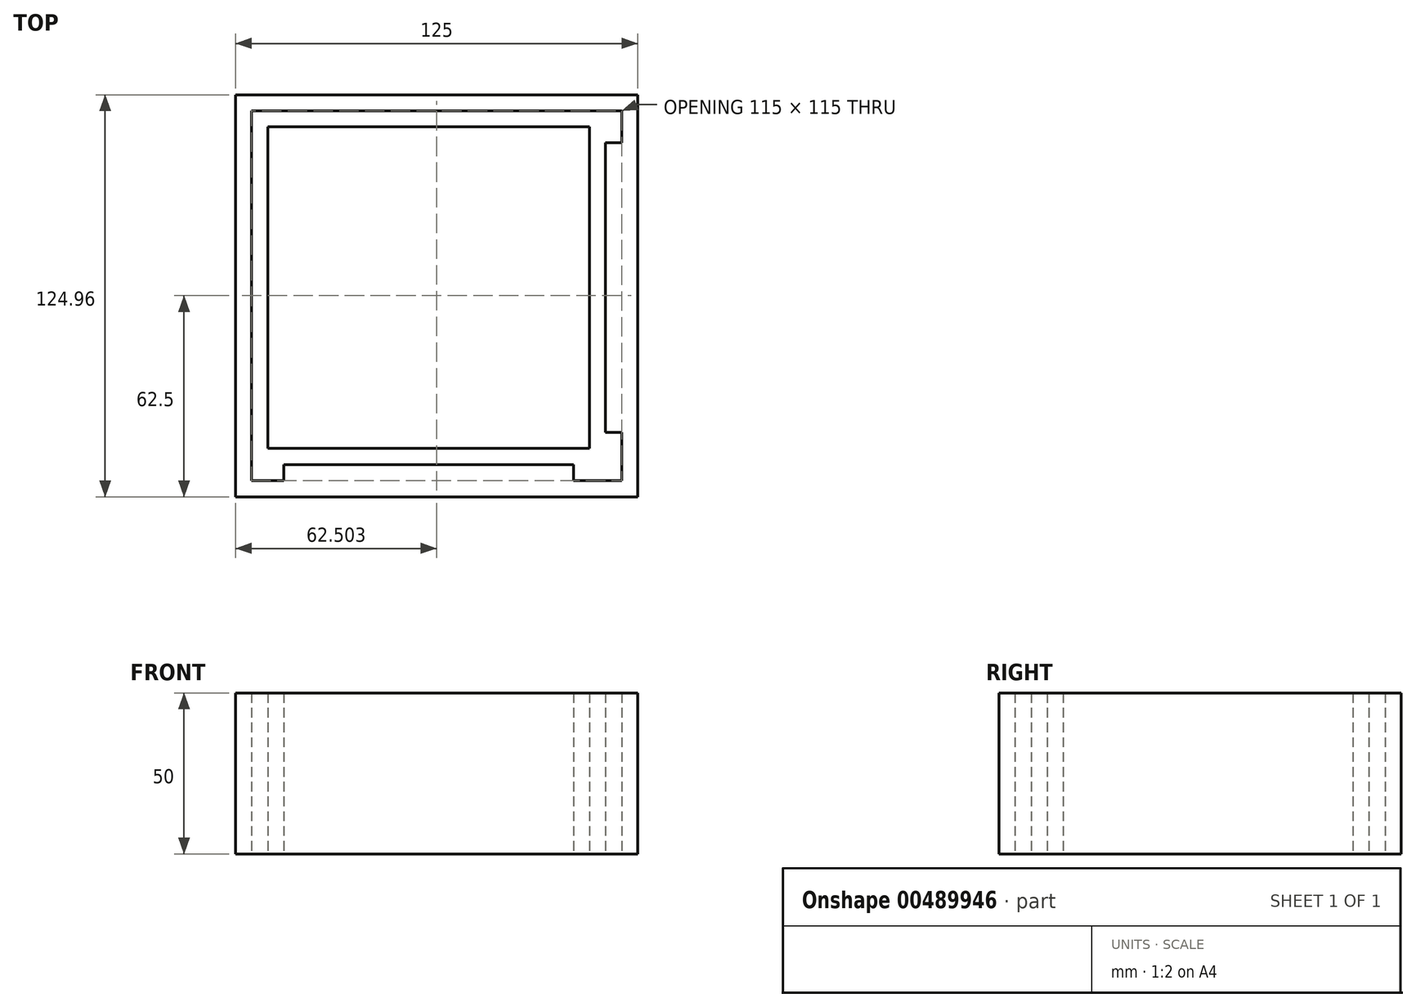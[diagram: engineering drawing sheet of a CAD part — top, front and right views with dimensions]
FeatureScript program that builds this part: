
annotation { "Feature Type Name" : "Feature", "Feature Type Description" : "" }
export const myFeature = defineFeature(function(context is Context, id is Id, definition is map)
    precondition{}
    {
        {
            var Q0;
            Q0=qCreatedBy(makeId("Top.planeOp"),FACE);
            var sketch = newSketch(context, id + "F0", { "sketchPlane" : qUnion([Q0])});
            skLineSegment(sketch, "E0.bottom", {"start": v(104.56, 35.9) * mm, "end": v(204.56, 35.9) * mm});
            skLineSegment(sketch, "E0.top", {"start": v(104.56, -64.1) * mm, "end": v(204.56, -64.1) * mm});
            skLineSegment(sketch, "E0.left", {"start": v(104.56, 35.9) * mm, "end": v(104.56, -64.1) * mm});
            skLineSegment(sketch, "E0.right", {"start": v(204.56, 35.9) * mm, "end": v(204.56, -64.1) * mm});
            skPoint(sketch, "E1", {"position": v(154.56, 35.9) * mm});
            skPoint(sketch, "E2", {"position": v(104.56, -14.1) * mm});
            skPoint(sketch, "E3", {"position": v(204.56, -14.1) * mm});
            skPoint(sketch, "E4", {"position": v(154.56, -64.1) * mm});
            skLineSegment(sketch, "E5", {"start": v(104.56, 35.9) * mm, "end": v(204.56, -64.1) * mm});
            skSolve(sketch);
        }
        {
            var Q0;
            Q0=qCreatedBy(makeId("Top.planeOp"),FACE);
            var sketch = newSketch(context, id + "F1", { "sketchPlane" : qUnion([Q0])});
            skLineSegment(sketch, "E6.bottom", {"start": v(99.56, 40.9) * mm, "end": v(214.56, 40.9) * mm});
            skLineSegment(sketch, "E6.left", {"start": v(99.56, 40.9) * mm, "end": v(99.56, -74.1) * mm});
            skPoint(sketch, "E7", {"position": v(154.56, -69.1) * mm});
            skPoint(sketch, "E8", {"position": v(159.56, 40.9) * mm});
            skLineSegment(sketch, "E9.bottom", {"start": v(209.56, 30.9) * mm, "end": v(214.56, 30.9) * mm});
            skLineSegment(sketch, "E9.top", {"start": v(209.56, -59.1) * mm, "end": v(214.56, -59.1) * mm});
            skLineSegment(sketch, "E9.left", {"start": v(209.56, 30.9) * mm, "end": v(209.56, -59.1) * mm});
            skLineSegment(sketch, "E9.right", {"start": v(214.56, 30.9) * mm, "end": v(214.56, -59.1) * mm});
            skPoint(sketch, "E10", {"position": v(209.56, -14.1) * mm});
            skLineSegment(sketch, "E11.MirrorCS", {"start": v(199.56, -69.1) * mm, "end": v(199.56, -74.1) * mm});
            skLineSegment(sketch, "E12.MirrorCS", {"start": v(109.56, -74.1) * mm, "end": v(199.56, -74.1) * mm});
            skLineSegment(sketch, "E13.MirrorCS", {"start": v(109.56, -69.1) * mm, "end": v(199.56, -69.1) * mm});
            skLineSegment(sketch, "E14.MirrorCS", {"start": v(109.56, -69.1) * mm, "end": v(109.56, -74.1) * mm});
            skLineSegment(sketch, "E15", {"start": v(99.56, -79.1) * mm, "end": v(219.56, -79.1) * mm});
            skLineSegment(sketch, "E16", {"start": v(219.56, 40.9) * mm, "end": v(219.56, -79.1) * mm});
            skLineSegment(sketch, "E17", {"start": v(99.56, -74.1) * mm, "end": v(214.56, -74.1) * mm});
            skLineSegment(sketch, "E18.MirrorCS", {"start": v(214.56, 40.9) * mm, "end": v(214.56, -74.1) * mm});
            skLineSegment(sketch, "E19.left", {"start": v(94.56, 40.9) * mm, "end": v(94.56, -79.1) * mm});
            skLineSegment(sketch, "E20", {"start": v(94.56, -79.1) * mm, "end": v(99.56, -79.1) * mm});
            skLineSegment(sketch, "E21.bottom", {"start": v(99.56, 45.86) * mm, "end": v(219.56, 45.86) * mm});
            skLineSegment(sketch, "E22", {"start": v(99.56, 45.86) * mm, "end": v(94.56, 45.86) * mm});
            skLineSegment(sketch, "E23", {"start": v(94.56, 45.86) * mm, "end": v(94.56, 40.9) * mm});
            skPoint(sketch, "E24.orphan", {"position": v(214.56, -79.1) * mm});
            skPoint(sketch, "E25.orphan", {"position": v(219.56, -74.1) * mm});
            skLineSegment(sketch, "E26", {"start": v(219.56, 45.86) * mm, "end": v(219.56, 40.9) * mm});
            skSolve(sketch);
        }
        {
            var Q0;
            Q0 = qSketchRegion(id + "F0", true);
            extrude(context, id + "F2", {"entities" : qUnion([Q0]), "depth" : 50 * mm, "offsetDistance" : 25 * mm});
        }
        {
            var Q0;
            {var subQ5=sQuery(id+"F1.wireOp",EDGE,"E6.bottom");Q0=makeQuery(id+"F1.imprint","IMPRINT",FACE,{"disambiguationData":[TD([[makeQuery(id+"F1.imprint","IMPRINT",EDGE,{"derivedFrom":subQ5}),1.0]])]});}
            var Q1;
            {var subQ0=sQuery(id+"F1.wireOp",EDGE,"E11.MirrorCS");Q1=makeQuery(id+"F1.imprint","IMPRINT",FACE,{"disambiguationData":[TD([[makeQuery(id+"F1.imprint","IMPRINT",EDGE,{"derivedFrom":subQ0}),-1.0]])]});}
            var Q2;
            {var subQ0=sQuery(id+"F1.wireOp",EDGE,"E9.bottom");Q2=makeQuery(id+"F1.imprint","IMPRINT",FACE,{"disambiguationData":[TD([[makeQuery(id+"F1.imprint","IMPRINT",EDGE,{"derivedFrom":subQ0}),-1.0]])]});}
            extrude(context, id + "F3", {"entities" : qUnion([Q0, Q1, Q2]), "depth" : 50 * mm, "offsetDistance" : 25 * mm});
        }
    });
